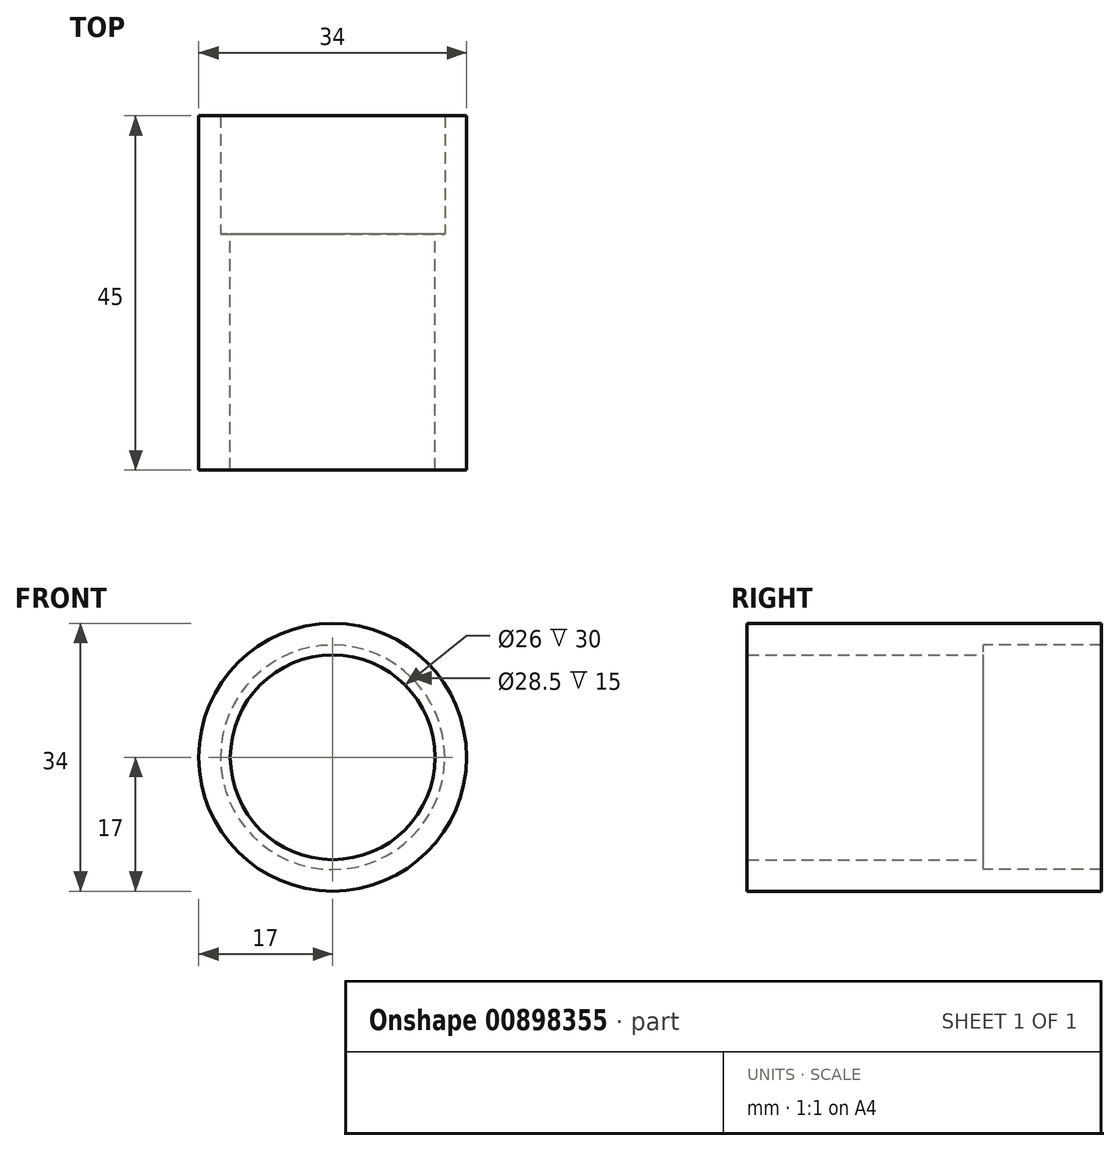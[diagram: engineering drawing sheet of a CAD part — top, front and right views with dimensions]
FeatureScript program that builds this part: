
annotation { "Feature Type Name" : "Feature", "Feature Type Description" : "" }
export const myFeature = defineFeature(function(context is Context, id is Id, definition is map)
    precondition{}
    {
        {
            var Q0;
            Q0=qCreatedBy(makeId("Front.planeOp"),FACE);
            var sketch = newSketch(context, id + "F0", { "sketchPlane" : qUnion([Q0])});
            skCircle(sketch, "E0", {"center": v(0, 0) * mm, "radius": 17 * mm});
            skCircle(sketch, "E1", {"center": v(0, 0) * mm, "radius": 13 * mm});
            skCircle(sketch, "E2", {"center": v(0, 0) * mm, "radius": 14.25 * mm});
            skSolve(sketch);
        }
        {
            var Q0;
            Q0=makeQuery(id+"F0.imprint","IMPRINT",FACE,{"disambiguationData":[TD([[makeQuery(id+"F0.imprint","IMPRINT",EDGE,{"derivedFrom":sQuery(id+"F0.wireOp",EDGE,"E0")}),1.0]])]});
            var Q1;
            Q1=makeQuery(id+"F0.imprint","IMPRINT",FACE,{"disambiguationData":[TD([[makeQuery(id+"F0.imprint","IMPRINT",EDGE,{"derivedFrom":sQuery(id+"F0.wireOp",EDGE,"E1")}),-1.0]])]});
            extrude(context, id + "F1", {"entities" : qUnion([Q0, Q1]), "depth" : 30 * mm, "offsetDistance" : 25.4 * mm});
        }
        {
            var Q0;
            Q0=makeQuery(id+"F0.imprint","IMPRINT",FACE,{"disambiguationData":[TD([[makeQuery(id+"F0.imprint","IMPRINT",EDGE,{"derivedFrom":sQuery(id+"F0.wireOp",EDGE,"E0")}),1.0]])]});
            extrude(context, id + "F2", {"entities" : qUnion([Q0]), "operationType" : NewBodyOperationType.ADD, "oppositeDirection" : true, "depth" : 15 * mm, "offsetDistance" : 25 * mm});
        }
    });
